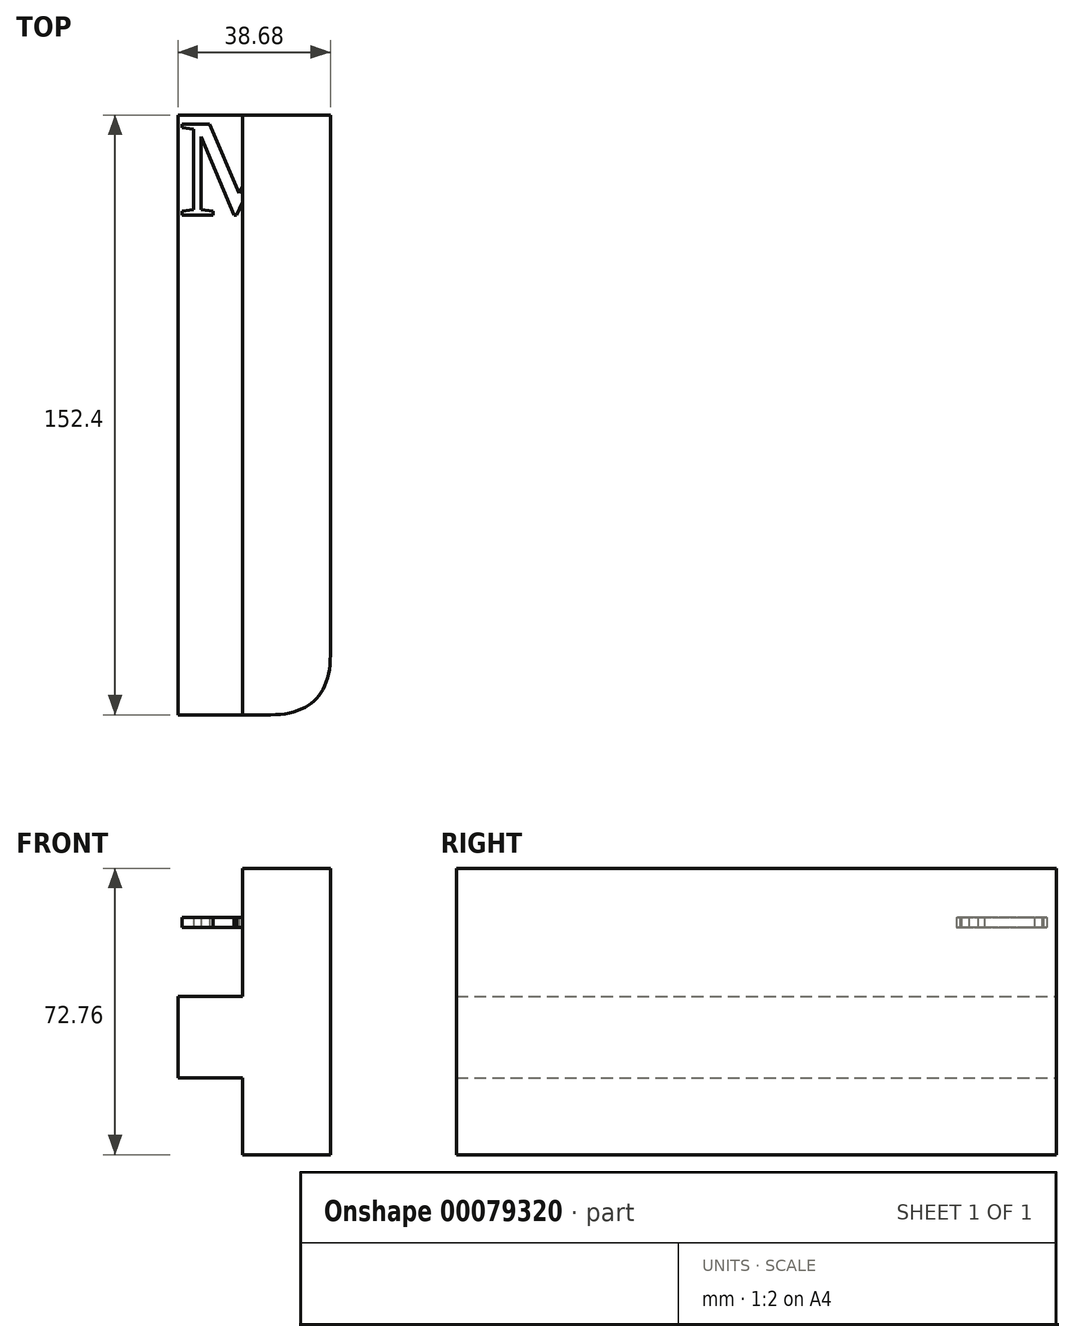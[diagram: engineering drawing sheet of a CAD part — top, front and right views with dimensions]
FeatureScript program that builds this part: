
annotation { "Feature Type Name" : "Feature", "Feature Type Description" : "" }
export const myFeature = defineFeature(function(context is Context, id is Id, definition is map)
    precondition{}
    {
        {
            var Q0;
            Q0=qCreatedBy(makeId("Top.planeOp"),FACE);
            var sketch = newSketch(context, id + "F0", { "sketchPlane" : qUnion([Q0])});
            skLineSegment(sketch, "E0", {"start": v(0, 0) * mm, "end": v(0, -25.4) * mm});
            skText(sketch, "E1", { "text": "M", "fontName": "Tinos-Regular.ttf"});
            const initialGuessF0  = {"E1": [0, -0.0254, 1, 0, 0.0254]};
            skSetInitialGuess(sketch, initialGuessF0);
            skSolve(sketch);
        }
        {
            var Q0;
            Q0 = qSketchRegion(id + "F0", true);
            extrude(context, id + "F1", {"entities" : qUnion([Q0]), "depth" : 2.54 * mm});
        }
        {
            var Q0;
            Q0=makeQuery(id+"F1.opExtrude","CAP_EDGE",EDGE,{"disambiguationData":[OSD([sQuery(id+"F0.wireOp",EDGE,"E1.sketch_text.stroke-17")])],"isStart":false});
            var Q1;
            Q1=makeQuery(id+"F1.opExtrude","CAP_EDGE",EDGE,{"disambiguationData":[OSD([sQuery(id+"F0.wireOp",EDGE,"E1.sketch_text.stroke-23")])],"isStart":false});
            chamfer(context, id + "F2", {"entities" : qUnion([Q0, Q1]), "width" : 0.25 * mm, "tangentPropagation" : true});
        }
        {
            var Q0;
            Q0=qCreatedBy(makeId("Front.planeOp"),FACE);
            var sketch = newSketch(context, id + "F3", { "sketchPlane" : qUnion([Q0])});
            skLineSegment(sketch, "E2.bottom", {"start": v(16.37, -38.24) * mm, "end": v(0, -38.24) * mm});
            skLineSegment(sketch, "E2.top", {"start": v(16.37, -17.5) * mm, "end": v(0, -17.5) * mm});
            skLineSegment(sketch, "E2.right", {"start": v(0, -38.24) * mm, "end": v(0, -17.5) * mm});
            skLineSegment(sketch, "E3.bottom", {"start": v(16.37, -57.7) * mm, "end": v(38.68, -57.7) * mm});
            skLineSegment(sketch, "E3.top", {"start": v(16.37, 15.06) * mm, "end": v(38.68, 15.06) * mm});
            skLineSegment(sketch, "E3.left", {"start": v(16.37, -57.7) * mm, "end": v(16.37, -38.24) * mm});
            skLineSegment(sketch, "E3.right", {"start": v(38.68, -57.7) * mm, "end": v(38.68, 15.06) * mm});
            skLineSegment(sketch, "E4.trimOffspring", {"start": v(16.37, -17.5) * mm, "end": v(16.37, 15.06) * mm});
            skSolve(sketch);
        }
        {
            var Q0;
            Q0=makeQuery(id+"F3.imprint","IMPRINT",FACE,{"disambiguationData":[TD([[makeQuery(id+"F3.imprint","IMPRINT",EDGE,{"derivedFrom":sQuery(id+"F3.wireOp",EDGE,"E2.bottom")}),-1.0]])]});
            extrude(context, id + "F4", {"entities" : qUnion([Q0]), "operationType" : NewBodyOperationType.ADD, "depth" : 152.4 * mm});
        }
        {
            var Q0;
            Q0=makeQuery(id+"F4.opExtrude","CAP_EDGE",EDGE,{"disambiguationData":[OSD([sQuery(id+"F3.wireOp",EDGE,"E3.right")])],"isStart":false});
            fillet(context, id + "F5", {"entities" : qUnion([Q0]), "radius" : 15.24 * mm, "tangentPropagation" : true, "rho" : 0.5, "crossSection" : FilletCrossSection.CONIC, "allowEdgeOverflow" : false});
        }
    });
